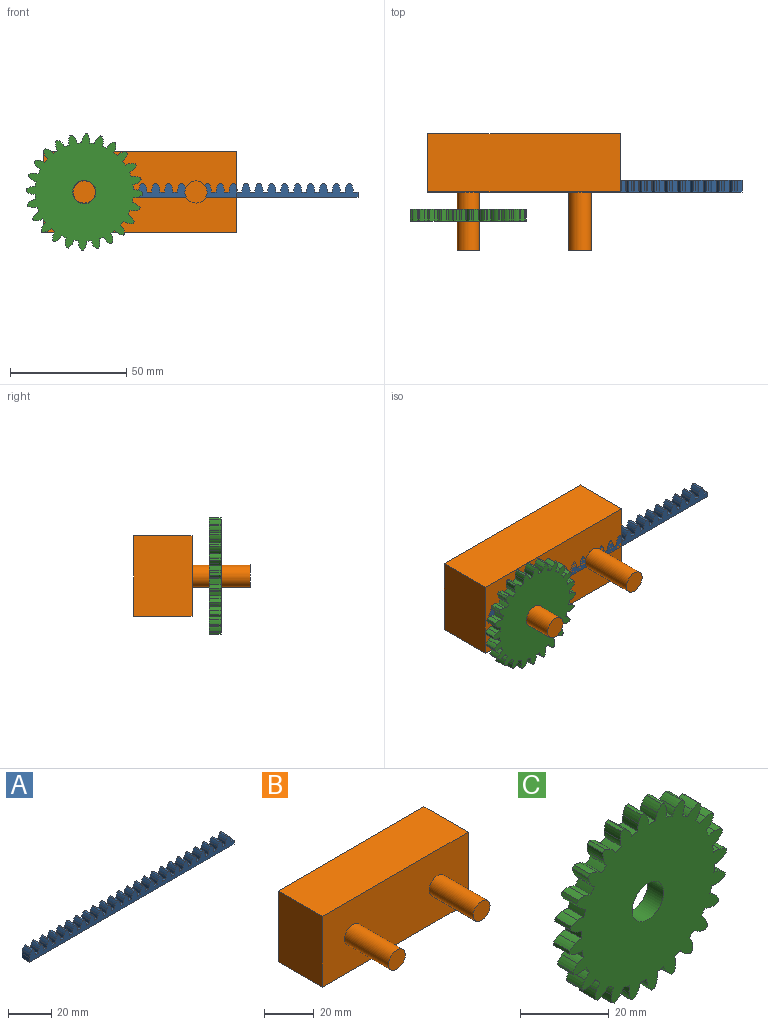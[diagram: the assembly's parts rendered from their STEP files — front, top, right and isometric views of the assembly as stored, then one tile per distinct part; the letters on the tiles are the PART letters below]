
ASSEMBLY  parts=3 mates=2
PART A: 173 faces, bbox 132.9x5x6.3 mm
  f0: cylinder r=5.39mm len=5mm, axis (0,1,0), area 10mm2, adj f1,f170,f171,f172
  f1: plane 5x2.01mm, normal (0,0,1), area 10mm2, adj f0,f2,f171,f172
  f2: plane 5x0mm, normal (1,0,0), area 0mm2, adj f1,f3,f171,f172
  f3: cylinder r=5.39mm len=5mm, axis (0,1,0), area 10mm2, adj f2,f4,f171,f172
  f4: cylinder r=6.11mm len=5mm, axis (0,1,0), area 11mm2, adj f3,f5,f171,f172
  f5: cylinder r=29.99mm len=5mm, axis (0,1,0), area 4.7mm2, adj f4,f6,f171,f172
  f6: cylinder r=6.16mm len=5mm, axis (0,1,0), area 11.1mm2, adj f5,f7,f171,f172
  f7: cylinder r=5.39mm len=5mm, axis (0,1,0), area 10mm2, adj f6,f8,f171,f172
  f8: plane 5x2.01mm, normal (0,0,1), area 10mm2, adj f7,f9,f171,f172
  f9: plane 5x0mm, normal (1,0,0), area 0mm2, adj f8,f10,f171,f172
  f10: cylinder r=5.39mm len=5mm, axis (0,1,0), area 10mm2, adj f9,f11,f171,f172
  f11: cylinder r=6.11mm len=5mm, axis (0,1,0), area 11mm2, adj f10,f12,f171,f172
  f12: cylinder r=29.99mm len=5mm, axis (0,1,0), area 4.7mm2, adj f11,f13,f171,f172
  f13: cylinder r=6.16mm len=5mm, axis (0,1,0), area 11.1mm2, adj f12,f14,f171,f172
  f14: cylinder r=5.39mm len=5mm, axis (0,1,0), area 10mm2, adj f13,f15,f171,f172
  f15: plane 5x2.01mm, normal (0,0,1), area 10mm2, adj f14,f16,f171,f172
  f16: plane 5x0mm, normal (1,0,0), area 0mm2, adj f15,f17,f171,f172
  f17: cylinder r=5.39mm len=5mm, axis (0,1,0), area 10mm2, adj f16,f18,f171,f172
  f18: cylinder r=6.11mm len=5mm, axis (0,1,0), area 11mm2, adj f17,f19,f171,f172
  f19: cylinder r=29.99mm len=5mm, axis (0,1,0), area 4.7mm2, adj f18,f20,f171,f172
  f20: cylinder r=6.16mm len=5mm, axis (0,1,0), area 11.1mm2, adj f19,f21,f171,f172
  f21: cylinder r=5.39mm len=5mm, axis (0,1,0), area 10mm2, adj f20,f22,f171,f172
  f22: plane 5x2.01mm, normal (0,0,1), area 10mm2, adj f21,f23,f171,f172
  f23: plane 5x0mm, normal (1,0,0), area 0mm2, adj f22,f24,f171,f172
  f24: cylinder r=5.39mm len=5mm, axis (0,1,0), area 10mm2, adj f23,f25,f171,f172
  f25: cylinder r=6.11mm len=5mm, axis (0,1,0), area 11mm2, adj f24,f26,f171,f172
  f26: cylinder r=29.99mm len=5mm, axis (0,1,0), area 4.7mm2, adj f25,f27,f171,f172
  f27: cylinder r=6.16mm len=5mm, axis (0,1,0), area 11.1mm2, adj f26,f28,f171,f172
  f28: cylinder r=5.39mm len=5mm, axis (0,1,0), area 10mm2, adj f27,f29,f171,f172
  f29: plane 5x2.01mm, normal (0,0,1), area 10mm2, adj f28,f30,f171,f172
  f30: plane 5x0mm, normal (1,0,0), area 0mm2, adj f29,f31,f171,f172
  f31: cylinder r=5.39mm len=5mm, axis (0,1,0), area 10mm2, adj f30,f32,f171,f172
  f32: cylinder r=6.11mm len=5mm, axis (0,1,0), area 11mm2, adj f31,f33,f171,f172
  f33: cylinder r=29.99mm len=5mm, axis (0,1,0), area 4.7mm2, adj f32,f34,f171,f172
  f34: cylinder r=6.16mm len=5mm, axis (0,1,0), area 11.1mm2, adj f33,f35,f171,f172
  f35: cylinder r=5.39mm len=5mm, axis (0,1,0), area 10mm2, adj f34,f36,f171,f172
  f36: plane 5x2.01mm, normal (0,0,1), area 10mm2, adj f35,f37,f171,f172
  f37: plane 5x0mm, normal (1,0,0), area 0mm2, adj f36,f38,f171,f172
  f38: cylinder r=5.39mm len=5mm, axis (0,1,0), area 10mm2, adj f37,f39,f171,f172
  f39: cylinder r=6.11mm len=5mm, axis (0,1,0), area 11mm2, adj f38,f40,f171,f172
  f40: cylinder r=29.99mm len=5mm, axis (0,1,0), area 4.7mm2, adj f39,f41,f171,f172
  f41: cylinder r=6.16mm len=5mm, axis (0,1,0), area 11.1mm2, adj f40,f42,f171,f172
  f42: cylinder r=5.39mm len=5mm, axis (0,1,0), area 10mm2, adj f41,f43,f171,f172
  f43: plane 5x2.01mm, normal (0,0,1), area 10mm2, adj f42,f44,f171,f172
  f44: plane 5x0mm, normal (1,0,0), area 0mm2, adj f43,f45,f171,f172
  f45: cylinder r=5.39mm len=5mm, axis (0,1,0), area 10mm2, adj f44,f46,f171,f172
  f46: cylinder r=6.11mm len=5mm, axis (0,1,0), area 11mm2, adj f45,f47,f171,f172
  f47: cylinder r=29.99mm len=5mm, axis (0,1,0), area 4.7mm2, adj f46,f48,f171,f172
  f48: cylinder r=6.16mm len=5mm, axis (0,1,0), area 11.1mm2, adj f47,f49,f171,f172
  f49: cylinder r=5.39mm len=5mm, axis (0,1,0), area 10mm2, adj f48,f50,f171,f172
  f50: plane 5x2.01mm, normal (0,0,1), area 10mm2, adj f49,f51,f171,f172
  f51: plane 5x0mm, normal (1,0,0), area 0mm2, adj f50,f52,f171,f172
  f52: cylinder r=5.39mm len=5mm, axis (0,1,0), area 10mm2, adj f51,f53,f171,f172
  f53: cylinder r=6.11mm len=5mm, axis (0,1,0), area 11mm2, adj f52,f54,f171,f172
  f54: cylinder r=29.99mm len=5mm, axis (0,1,0), area 4.7mm2, adj f53,f55,f171,f172
  f55: cylinder r=6.16mm len=5mm, axis (0,1,0), area 11.1mm2, adj f54,f56,f171,f172
  f56: cylinder r=5.39mm len=5mm, axis (0,1,0), area 10mm2, adj f55,f57,f171,f172
  f57: plane 5x2.01mm, normal (0,0,1), area 10mm2, adj f56,f58,f171,f172
  f58: plane 5x0mm, normal (1,0,0), area 0mm2, adj f57,f59,f171,f172
  f59: cylinder r=5.39mm len=5mm, axis (0,1,0), area 10mm2, adj f58,f60,f171,f172
  f60: cylinder r=6.11mm len=5mm, axis (0,1,0), area 11mm2, adj f59,f61,f171,f172
  f61: cylinder r=29.99mm len=5mm, axis (0,1,0), area 4.7mm2, adj f60,f62,f171,f172
  f62: cylinder r=6.16mm len=5mm, axis (0,1,0), area 11.1mm2, adj f61,f63,f171,f172
  f63: cylinder r=5.39mm len=5mm, axis (0,1,0), area 10mm2, adj f62,f64,f171,f172
  f64: plane 5x2.01mm, normal (0,0,1), area 10mm2, adj f63,f65,f171,f172
  f65: plane 5x0mm, normal (1,0,0), area 0mm2, adj f64,f66,f171,f172
  f66: cylinder r=5.39mm len=5mm, axis (0,1,0), area 10mm2, adj f65,f67,f171,f172
  f67: cylinder r=6.11mm len=5mm, axis (0,1,0), area 11mm2, adj f66,f68,f171,f172
  f68: cylinder r=29.99mm len=5mm, axis (0,1,0), area 4.7mm2, adj f67,f69,f171,f172
  f69: cylinder r=6.16mm len=5mm, axis (0,1,0), area 11.1mm2, adj f68,f70,f171,f172
  f70: cylinder r=5.39mm len=5mm, axis (0,1,0), area 10mm2, adj f69,f71,f171,f172
  f71: plane 5x2.01mm, normal (0,0,1), area 10mm2, adj f70,f72,f171,f172
  f72: plane 5x0mm, normal (1,0,0), area 0mm2, adj f71,f73,f171,f172
  f73: cylinder r=5.39mm len=5mm, axis (0,1,0), area 10mm2, adj f72,f74,f171,f172
  f74: cylinder r=6.11mm len=5mm, axis (0,1,0), area 11mm2, adj f73,f75,f171,f172
  f75: cylinder r=29.99mm len=5mm, axis (0,1,0), area 4.7mm2, adj f74,f76,f171,f172
  f76: cylinder r=6.16mm len=5mm, axis (0,1,0), area 11.1mm2, adj f75,f77,f171,f172
  f77: cylinder r=5.39mm len=5mm, axis (0,1,0), area 10mm2, adj f76,f78,f171,f172
  f78: plane 5x2.01mm, normal (0,0,1), area 10mm2, adj f77,f79,f171,f172
  f79: plane 5x0mm, normal (1,0,0), area 0mm2, adj f78,f80,f171,f172
  f80: cylinder r=5.39mm len=5mm, axis (0,1,0), area 10mm2, adj f79,f81,f171,f172
  f81: cylinder r=6.11mm len=5mm, axis (0,1,0), area 11mm2, adj f80,f82,f171,f172
  f82: cylinder r=29.99mm len=5mm, axis (0,1,0), area 4.7mm2, adj f81,f83,f171,f172
  f83: cylinder r=6.16mm len=5mm, axis (0,1,0), area 11.1mm2, adj f82,f84,f171,f172
  f84: cylinder r=5.39mm len=5mm, axis (0,1,0), area 10mm2, adj f83,f85,f171,f172
  f85: plane 5x2.01mm, normal (0,0,1), area 10mm2, adj f84,f86,f171,f172
  f86: plane 5x0mm, normal (1,0,0), area 0mm2, adj f85,f87,f171,f172
  f87: cylinder r=5.39mm len=5mm, axis (0,1,0), area 10mm2, adj f86,f88,f171,f172
  f88: cylinder r=6.11mm len=5mm, axis (0,1,0), area 11mm2, adj f87,f89,f171,f172
  f89: cylinder r=29.99mm len=5mm, axis (0,1,0), area 4.7mm2, adj f88,f90,f171,f172
  f90: cylinder r=6.16mm len=5mm, axis (0,1,0), area 11.1mm2, adj f89,f91,f171,f172
  f91: cylinder r=5.39mm len=5mm, axis (0,1,0), area 10mm2, adj f90,f92,f171,f172
  f92: plane 5x2.01mm, normal (0,0,1), area 10mm2, adj f91,f93,f171,f172
  f93: plane 5x0mm, normal (1,0,0), area 0mm2, adj f92,f94,f171,f172
  f94: cylinder r=5.39mm len=5mm, axis (0,1,0), area 10mm2, adj f93,f95,f171,f172
  f95: cylinder r=6.11mm len=5mm, axis (0,1,0), area 11mm2, adj f94,f96,f171,f172
  f96: cylinder r=29.99mm len=5mm, axis (0,1,0), area 4.7mm2, adj f95,f97,f171,f172
  f97: cylinder r=6.16mm len=5mm, axis (0,1,0), area 11.1mm2, adj f96,f98,f171,f172
  f98: cylinder r=5.39mm len=5mm, axis (0,1,0), area 10mm2, adj f97,f99,f171,f172
  f99: plane 5x2.01mm, normal (0,0,1), area 10mm2, adj f98,f100,f171,f172
  f100: plane 5x0mm, normal (1,0,0), area 0mm2, adj f99,f101,f171,f172
  f101: cylinder r=5.39mm len=5mm, axis (0,1,0), area 10mm2, adj f100,f102,f171,f172
  f102: cylinder r=6.11mm len=5mm, axis (0,1,0), area 11mm2, adj f101,f103,f171,f172
  f103: cylinder r=29.99mm len=5mm, axis (0,1,0), area 4.7mm2, adj f102,f104,f171,f172
  f104: cylinder r=6.16mm len=5mm, axis (0,1,0), area 11.1mm2, adj f103,f105,f171,f172
  f105: cylinder r=5.39mm len=5mm, axis (0,1,0), area 10mm2, adj f104,f106,f171,f172
  f106: plane 5x2.01mm, normal (0,0,1), area 10mm2, adj f105,f107,f171,f172
  f107: plane 5x0mm, normal (1,0,0), area 0mm2, adj f106,f108,f171,f172
  f108: cylinder r=5.39mm len=5mm, axis (0,1,0), area 10mm2, adj f107,f109,f171,f172
  f109: cylinder r=6.11mm len=5mm, axis (0,1,0), area 11mm2, adj f108,f110,f171,f172
  f110: cylinder r=29.99mm len=5mm, axis (0,1,0), area 4.7mm2, adj f109,f111,f171,f172
  f111: cylinder r=6.16mm len=5mm, axis (0,1,0), area 11.1mm2, adj f110,f112,f171,f172
  f112: cylinder r=5.39mm len=5mm, axis (0,1,0), area 10mm2, adj f111,f113,f171,f172
  f113: plane 5x2.01mm, normal (0,0,1), area 10mm2, adj f112,f114,f171,f172
  f114: plane 5x0mm, normal (1,0,0), area 0mm2, adj f113,f115,f171,f172
  f115: cylinder r=5.39mm len=5mm, axis (0,1,0), area 10mm2, adj f114,f116,f171,f172
  f116: cylinder r=6.11mm len=5mm, axis (0,1,0), area 11mm2, adj f115,f117,f171,f172
  f117: cylinder r=29.99mm len=5mm, axis (0,1,0), area 4.7mm2, adj f116,f118,f171,f172
  f118: cylinder r=6.16mm len=5mm, axis (0,1,0), area 11.1mm2, adj f117,f119,f171,f172
  f119: cylinder r=5.39mm len=5mm, axis (0,1,0), area 10mm2, adj f118,f120,f171,f172
  f120: plane 5x2.01mm, normal (0,0,1), area 10mm2, adj f119,f121,f171,f172
  f121: plane 5x0mm, normal (1,0,0), area 0mm2, adj f120,f122,f171,f172
  f122: cylinder r=5.39mm len=5mm, axis (0,1,0), area 10mm2, adj f121,f123,f171,f172
  f123: cylinder r=6.11mm len=5mm, axis (0,1,0), area 11mm2, adj f122,f124,f171,f172
  f124: cylinder r=29.99mm len=5mm, axis (0,1,0), area 4.7mm2, adj f123,f125,f171,f172
  f125: cylinder r=6.16mm len=5mm, axis (0,1,0), area 11.1mm2, adj f124,f126,f171,f172
  f126: cylinder r=5.39mm len=5mm, axis (0,1,0), area 10mm2, adj f125,f127,f171,f172
  f127: plane 5x2.01mm, normal (0,0,1), area 10mm2, adj f126,f128,f171,f172
  f128: plane 5x0mm, normal (1,0,0), area 0mm2, adj f127,f129,f171,f172
  f129: cylinder r=5.39mm len=5mm, axis (0,1,0), area 10mm2, adj f128,f130,f171,f172
  f130: cylinder r=6.11mm len=5mm, axis (0,1,0), area 11mm2, adj f129,f131,f171,f172
  f131: cylinder r=29.99mm len=5mm, axis (0,1,0), area 4.7mm2, adj f130,f132,f171,f172
  f132: cylinder r=6.16mm len=5mm, axis (0,1,0), area 11.1mm2, adj f131,f133,f171,f172
  f133: cylinder r=5.39mm len=5mm, axis (0,1,0), area 10mm2, adj f132,f134,f171,f172
  f134: plane 5x2.01mm, normal (0,0,1), area 10mm2, adj f133,f135,f171,f172
  f135: plane 5x0mm, normal (1,0,0), area 0mm2, adj f134,f136,f171,f172
  f136: cylinder r=5.39mm len=5mm, axis (0,1,0), area 10mm2, adj f135,f137,f171,f172
  f137: cylinder r=6.11mm len=5mm, axis (0,1,0), area 11mm2, adj f136,f138,f171,f172
  f138: cylinder r=29.99mm len=5mm, axis (0,1,0), area 4.7mm2, adj f137,f139,f171,f172
  f139: cylinder r=6.16mm len=5mm, axis (0,1,0), area 11.1mm2, adj f138,f140,f171,f172
  f140: cylinder r=5.39mm len=5mm, axis (0,1,0), area 10mm2, adj f139,f141,f171,f172
  f141: plane 5x2.01mm, normal (0,0,1), area 10mm2, adj f140,f142,f171,f172
  f142: plane 5x0mm, normal (1,0,0), area 0mm2, adj f141,f143,f171,f172
  f143: cylinder r=5.39mm len=5mm, axis (0,1,0), area 10mm2, adj f142,f144,f171,f172
  f144: cylinder r=6.11mm len=5mm, axis (0,1,0), area 11mm2, adj f143,f145,f171,f172
  f145: cylinder r=29.99mm len=5mm, axis (0,1,0), area 4.7mm2, adj f144,f146,f171,f172
  f146: cylinder r=6.16mm len=5mm, axis (0,1,0), area 11.1mm2, adj f145,f147,f171,f172
  f147: cylinder r=5.39mm len=5mm, axis (0,1,0), area 10mm2, adj f146,f148,f171,f172
  f148: plane 5x2.01mm, normal (0,0,1), area 10mm2, adj f147,f149,f171,f172
  f149: plane 5x0mm, normal (1,0,0), area 0mm2, adj f148,f150,f171,f172
  f150: cylinder r=5.39mm len=5mm, axis (0,1,0), area 10mm2, adj f149,f151,f171,f172
  f151: cylinder r=6.11mm len=5mm, axis (0,1,0), area 11mm2, adj f150,f152,f171,f172
  f152: cylinder r=29.99mm len=5mm, axis (0,1,0), area 4.7mm2, adj f151,f153,f171,f172
  f153: cylinder r=6.16mm len=5mm, axis (0,1,0), area 11.1mm2, adj f152,f154,f171,f172
  f154: cylinder r=5.39mm len=5mm, axis (0,1,0), area 10mm2, adj f153,f155,f171,f172
  f155: plane 5x2.01mm, normal (0,0,1), area 10mm2, adj f154,f156,f171,f172
  f156: plane 5x0mm, normal (1,0,0), area 0mm2, adj f155,f157,f171,f172
  f157: cylinder r=5.39mm len=5mm, axis (0,1,0), area 10mm2, adj f156,f158,f171,f172
  f158: cylinder r=6.11mm len=5mm, axis (0,1,0), area 11mm2, adj f157,f159,f171,f172
  f159: cylinder r=29.99mm len=5mm, axis (0,1,0), area 4.7mm2, adj f158,f160,f171,f172
  f160: cylinder r=6.16mm len=5mm, axis (0,1,0), area 11.1mm2, adj f159,f161,f171,f172
  f161: cylinder r=5.39mm len=5mm, axis (0,1,0), area 10mm2, adj f160,f162,f171,f172
  f162: plane 5x2.34mm, normal (-1,0,0), area 11.7mm2, adj f161,f163,f171,f172
  f163: plane 132.89x5mm, normal (0,0,-1), area 664.4mm2, adj f162,f164,f171,f172
  f164: plane 5x2.23mm, normal (1,0,0), area 11.1mm2, adj f163,f165,f171,f172
  f165: plane 5x2.01mm, normal (0,0,1), area 10mm2, adj f164,f166,f171,f172
  f166: plane 5x0mm, normal (1,0,0), area 0mm2, adj f165,f167,f171,f172
  f167: cylinder r=5.39mm len=5mm, axis (0,1,0), area 10mm2, adj f166,f168,f171,f172
  f168: cylinder r=6.11mm len=5mm, axis (0,1,0), area 11mm2, adj f167,f169,f171,f172
  f169: cylinder r=29.99mm len=5mm, axis (0,1,0), area 4.7mm2, adj f168,f170,f171,f172
  f170: cylinder r=6.16mm len=5mm, axis (0,1,0), area 11.1mm2, adj f0,f169,f171,f172
  f171: plane 132.9x6.26mm, normal (0,-1,0), area 563.7mm2, adj f0,f1,f2,f3,f4,f5,f6,f7
  f172: plane 132.9x6.26mm, normal (0,1,0), area 563.7mm2, adj f0,f1,f2,f3,f4,f5,f6,f7
PART B: 10 faces, bbox 82.7x50x34.7 mm
  f0: plane 82.71x25mm, normal (0,0,-1), area 2067.7mm2, adj f1,f3,f4,f5
  f1: plane 34.71x25mm, normal (1,0,0), area 867.7mm2, adj f0,f2,f4,f5
  f2: plane 82.71x25mm, normal (0,0,1), area 2067.7mm2, adj f1,f3,f4,f5
  f3: plane 34.71x25mm, normal (-1,0,0), area 867.7mm2, adj f0,f2,f4,f5
  f4: plane 82.71x34.71mm, normal (0,-1,0), area 2728.7mm2, adj f0,f1,f2,f3,f6,f8
  f5: plane 82.71x34.71mm, normal (0,1,0), area 2870.4mm2, adj f0,f1,f2,f3
  f6: cylinder r=4.75mm len=25mm, axis (0,1,0), area 746.1mm2, adj f4,f7
  f7: plane 9.5x9.5mm, normal (0,-1,0), area 70.9mm2, adj f6
  f8: cylinder r=4.75mm len=25mm, axis (0,1,0), area 746.1mm2, adj f4,f9
  f9: plane 9.5x9.5mm, normal (0,-1,0), area 70.9mm2, adj f8
PART C: 147 faces, bbox 49.9x5x49.9 mm
  f0: cylinder r=21.15mm len=5mm, axis (0,1,0), area 10mm2, adj f29,f30,f31,f91
  f1: cylinder r=21.15mm len=5mm, axis (0,1,0), area 10mm2, adj f30,f31,f86,f90
  f2: cylinder r=21.15mm len=5mm, axis (0,1,0), area 10mm2, adj f30,f31,f81,f85
  f3: cylinder r=21.15mm len=5mm, axis (0,1,0), area 10mm2, adj f30,f31,f76,f80
  f4: cylinder r=21.15mm len=5mm, axis (0,1,0), area 10mm2, adj f30,f31,f71,f75
  f5: cylinder r=21.15mm len=5mm, axis (0,1,0), area 10mm2, adj f30,f31,f66,f70
  f6: cylinder r=21.15mm len=5mm, axis (0,1,0), area 10mm2, adj f30,f31,f61,f65
  f7: cylinder r=21.15mm len=5mm, axis (0,1,0), area 10mm2, adj f30,f31,f56,f60
  f8: cylinder r=21.15mm len=5mm, axis (0,1,0), area 10mm2, adj f30,f31,f51,f55
  f9: cylinder r=21.15mm len=5mm, axis (0,1,0), area 10mm2, adj f30,f31,f46,f50
  f10: cylinder r=21.15mm len=5mm, axis (0,1,0), area 10mm2, adj f30,f31,f41,f45
  f11: cylinder r=21.15mm len=5mm, axis (0,1,0), area 10mm2, adj f30,f31,f36,f40
  f12: cylinder r=21.15mm len=5mm, axis (0,1,0), area 10mm2, adj f30,f31,f35,f142
  f13: cylinder r=21.15mm len=5mm, axis (0,1,0), area 10mm2, adj f30,f31,f141,f146
  f14: cylinder r=21.15mm len=5mm, axis (0,1,0), area 10mm2, adj f30,f31,f136,f140
  f15: cylinder r=21.15mm len=5mm, axis (0,1,0), area 10mm2, adj f30,f31,f131,f135
  f16: cylinder r=21.15mm len=5mm, axis (0,1,0), area 10mm2, adj f30,f31,f126,f130
  f17: cylinder r=21.15mm len=5mm, axis (0,1,0), area 10mm2, adj f30,f31,f121,f125
  f18: cylinder r=21.15mm len=5mm, axis (0,1,0), area 10mm2, adj f30,f31,f116,f120
  f19: cylinder r=21.15mm len=5mm, axis (0,1,0), area 10mm2, adj f30,f31,f111,f115
  f20: cylinder r=21.15mm len=5mm, axis (0,1,0), area 10mm2, adj f30,f31,f106,f110
  f21: cylinder r=21.15mm len=5mm, axis (0,1,0), area 10mm2, adj f30,f31,f101,f105
  f22: cylinder r=21.15mm len=5mm, axis (0,1,0), area 10mm2, adj f30,f31,f95,f100
  f23: cylinder r=21.15mm len=5mm, axis (0,1,0), area 10mm2, adj f24,f30,f31,f96
  f24: cylinder r=5.39mm len=5mm, axis (0,1,0), area 10mm2, adj f23,f25,f30,f31
  f25: cylinder r=6.11mm len=5mm, axis (0,1,0), area 11mm2, adj f24,f26,f30,f31
  f26: cylinder r=29.99mm len=5mm, axis (0,1,0), area 4.7mm2, adj f25,f27,f30,f31
  f27: cylinder r=6.16mm len=5mm, axis (0,1,0), area 11.1mm2, adj f26,f29,f30,f31
  f28: cylinder r=5mm len=10mm, axis (0,1,0), area 157.1mm2, adj f30,f31
  f29: cylinder r=5.39mm len=5mm, axis (0,1,0), area 10mm2, adj f0,f27,f30,f31
  f30: plane 49.91x49.91mm, normal (0,-1,0), area 1582.5mm2, adj f0,f1,f2,f3,f4,f5,f6,f7
  f31: plane 49.91x49.91mm, normal (0,1,0), area 1582.5mm2, adj f0,f1,f2,f3,f4,f5,f6,f7
  f32: cylinder r=6.11mm len=5mm, axis (0,1,0), area 11mm2, adj f30,f31,f33,f36
  f33: cylinder r=29.99mm len=5mm, axis (0,1,0), area 4.7mm2, adj f30,f31,f32,f34
  f34: cylinder r=6.16mm len=5mm, axis (0,1,0), area 11.1mm2, adj f30,f31,f33,f35
  f35: cylinder r=5.39mm len=5mm, axis (0,1,0), area 10mm2, adj f12,f30,f31,f34
  f36: cylinder r=5.39mm len=5mm, axis (0,1,0), area 10mm2, adj f11,f30,f31,f32
  f37: cylinder r=6.11mm len=5mm, axis (0,1,0), area 11mm2, adj f30,f31,f38,f41
  f38: cylinder r=29.99mm len=5mm, axis (0,1,0), area 4.7mm2, adj f30,f31,f37,f39
  f39: cylinder r=6.16mm len=5mm, axis (0,1,0), area 11.1mm2, adj f30,f31,f38,f40
  f40: cylinder r=5.39mm len=5mm, axis (0,1,0), area 10mm2, adj f11,f30,f31,f39
  f41: cylinder r=5.39mm len=5mm, axis (0,1,0), area 10mm2, adj f10,f30,f31,f37
  f42: cylinder r=6.11mm len=5mm, axis (0,1,0), area 11mm2, adj f30,f31,f43,f46
  f43: cylinder r=29.99mm len=5mm, axis (0,1,0), area 4.7mm2, adj f30,f31,f42,f44
  f44: cylinder r=6.16mm len=5mm, axis (0,1,0), area 11.1mm2, adj f30,f31,f43,f45
  f45: cylinder r=5.39mm len=5mm, axis (0,1,0), area 10mm2, adj f10,f30,f31,f44
  f46: cylinder r=5.39mm len=5mm, axis (0,1,0), area 10mm2, adj f9,f30,f31,f42
  f47: cylinder r=6.11mm len=5mm, axis (0,1,0), area 11mm2, adj f30,f31,f48,f51
  f48: cylinder r=29.99mm len=5mm, axis (0,1,0), area 4.7mm2, adj f30,f31,f47,f49
  f49: cylinder r=6.16mm len=5mm, axis (0,1,0), area 11.1mm2, adj f30,f31,f48,f50
  f50: cylinder r=5.39mm len=5mm, axis (0,1,0), area 10mm2, adj f9,f30,f31,f49
  f51: cylinder r=5.39mm len=5mm, axis (0,1,0), area 10mm2, adj f8,f30,f31,f47
  f52: cylinder r=6.11mm len=5mm, axis (0,1,0), area 11mm2, adj f30,f31,f53,f56
  f53: cylinder r=29.99mm len=5mm, axis (0,1,0), area 4.7mm2, adj f30,f31,f52,f54
  f54: cylinder r=6.16mm len=5mm, axis (0,1,0), area 11.1mm2, adj f30,f31,f53,f55
  f55: cylinder r=5.39mm len=5mm, axis (0,1,0), area 10mm2, adj f8,f30,f31,f54
  f56: cylinder r=5.39mm len=5mm, axis (0,1,0), area 10mm2, adj f7,f30,f31,f52
  f57: cylinder r=6.11mm len=5mm, axis (0,1,0), area 11mm2, adj f30,f31,f58,f61
  f58: cylinder r=29.99mm len=5mm, axis (0,1,0), area 4.7mm2, adj f30,f31,f57,f59
  f59: cylinder r=6.16mm len=5mm, axis (0,1,0), area 11.1mm2, adj f30,f31,f58,f60
  f60: cylinder r=5.39mm len=5mm, axis (0,1,0), area 10mm2, adj f7,f30,f31,f59
  f61: cylinder r=5.39mm len=5mm, axis (0,1,0), area 10mm2, adj f6,f30,f31,f57
  f62: cylinder r=6.11mm len=5mm, axis (0,1,0), area 11mm2, adj f30,f31,f63,f66
  f63: cylinder r=29.99mm len=5mm, axis (0,1,0), area 4.7mm2, adj f30,f31,f62,f64
  f64: cylinder r=6.16mm len=5mm, axis (0,1,0), area 11.1mm2, adj f30,f31,f63,f65
  f65: cylinder r=5.39mm len=5mm, axis (0,1,0), area 10mm2, adj f6,f30,f31,f64
  f66: cylinder r=5.39mm len=5mm, axis (0,1,0), area 10mm2, adj f5,f30,f31,f62
  f67: cylinder r=6.11mm len=5mm, axis (0,1,0), area 11mm2, adj f30,f31,f68,f71
  f68: cylinder r=29.99mm len=5mm, axis (0,1,0), area 4.7mm2, adj f30,f31,f67,f69
  f69: cylinder r=6.16mm len=5mm, axis (0,1,0), area 11.1mm2, adj f30,f31,f68,f70
  f70: cylinder r=5.39mm len=5mm, axis (0,1,0), area 10mm2, adj f5,f30,f31,f69
  f71: cylinder r=5.39mm len=5mm, axis (0,1,0), area 10mm2, adj f4,f30,f31,f67
  f72: cylinder r=6.11mm len=5mm, axis (0,1,0), area 11mm2, adj f30,f31,f73,f76
  f73: cylinder r=29.99mm len=5mm, axis (0,1,0), area 4.7mm2, adj f30,f31,f72,f74
  f74: cylinder r=6.16mm len=5mm, axis (0,1,0), area 11.1mm2, adj f30,f31,f73,f75
  f75: cylinder r=5.39mm len=5mm, axis (0,1,0), area 10mm2, adj f4,f30,f31,f74
  f76: cylinder r=5.39mm len=5mm, axis (0,1,0), area 10mm2, adj f3,f30,f31,f72
  f77: cylinder r=6.11mm len=5mm, axis (0,1,0), area 11mm2, adj f30,f31,f78,f81
  f78: cylinder r=29.99mm len=5mm, axis (0,1,0), area 4.7mm2, adj f30,f31,f77,f79
  f79: cylinder r=6.16mm len=5mm, axis (0,1,0), area 11.1mm2, adj f30,f31,f78,f80
  f80: cylinder r=5.39mm len=5mm, axis (0,1,0), area 10mm2, adj f3,f30,f31,f79
  f81: cylinder r=5.39mm len=5mm, axis (0,1,0), area 10mm2, adj f2,f30,f31,f77
  f82: cylinder r=6.11mm len=5mm, axis (0,1,0), area 11mm2, adj f30,f31,f83,f86
  f83: cylinder r=29.99mm len=5mm, axis (0,1,0), area 4.7mm2, adj f30,f31,f82,f84
  f84: cylinder r=6.16mm len=5mm, axis (0,1,0), area 11.1mm2, adj f30,f31,f83,f85
  f85: cylinder r=5.39mm len=5mm, axis (0,1,0), area 10mm2, adj f2,f30,f31,f84
  f86: cylinder r=5.39mm len=5mm, axis (0,1,0), area 10mm2, adj f1,f30,f31,f82
  f87: cylinder r=6.11mm len=5mm, axis (0,1,0), area 11mm2, adj f30,f31,f88,f91
  f88: cylinder r=29.99mm len=5mm, axis (0,1,0), area 4.7mm2, adj f30,f31,f87,f89
  f89: cylinder r=6.16mm len=5mm, axis (0,1,0), area 11.1mm2, adj f30,f31,f88,f90
  f90: cylinder r=5.39mm len=5mm, axis (0,1,0), area 10mm2, adj f1,f30,f31,f89
  f91: cylinder r=5.39mm len=5mm, axis (0,1,0), area 10mm2, adj f0,f30,f31,f87
  f92: cylinder r=6.11mm len=5mm, axis (0,1,0), area 11mm2, adj f30,f31,f93,f95
  f93: cylinder r=29.99mm len=5mm, axis (0,1,0), area 4.7mm2, adj f30,f31,f92,f94
  f94: cylinder r=6.16mm len=5mm, axis (0,1,0), area 11.1mm2, adj f30,f31,f93,f96
  f95: cylinder r=5.39mm len=5mm, axis (0,1,0), area 10mm2, adj f22,f30,f31,f92
  f96: cylinder r=5.39mm len=5mm, axis (0,1,0), area 10mm2, adj f23,f30,f31,f94
  f97: cylinder r=6.11mm len=5mm, axis (0,1,0), area 11mm2, adj f30,f31,f98,f101
  f98: cylinder r=29.99mm len=5mm, axis (0,1,0), area 4.7mm2, adj f30,f31,f97,f99
  f99: cylinder r=6.16mm len=5mm, axis (0,1,0), area 11.1mm2, adj f30,f31,f98,f100
  f100: cylinder r=5.39mm len=5mm, axis (0,1,0), area 10mm2, adj f22,f30,f31,f99
  f101: cylinder r=5.39mm len=5mm, axis (0,1,0), area 10mm2, adj f21,f30,f31,f97
  f102: cylinder r=6.11mm len=5mm, axis (0,1,0), area 11mm2, adj f30,f31,f103,f106
  f103: cylinder r=29.99mm len=5mm, axis (0,1,0), area 4.7mm2, adj f30,f31,f102,f104
  f104: cylinder r=6.16mm len=5mm, axis (0,1,0), area 11.1mm2, adj f30,f31,f103,f105
  f105: cylinder r=5.39mm len=5mm, axis (0,1,0), area 10mm2, adj f21,f30,f31,f104
  f106: cylinder r=5.39mm len=5mm, axis (0,1,0), area 10mm2, adj f20,f30,f31,f102
  f107: cylinder r=6.11mm len=5mm, axis (0,1,0), area 11mm2, adj f30,f31,f108,f111
  f108: cylinder r=29.99mm len=5mm, axis (0,1,0), area 4.7mm2, adj f30,f31,f107,f109
  f109: cylinder r=6.16mm len=5mm, axis (0,1,0), area 11.1mm2, adj f30,f31,f108,f110
  f110: cylinder r=5.39mm len=5mm, axis (0,1,0), area 10mm2, adj f20,f30,f31,f109
  f111: cylinder r=5.39mm len=5mm, axis (0,1,0), area 10mm2, adj f19,f30,f31,f107
  f112: cylinder r=6.11mm len=5mm, axis (0,1,0), area 11mm2, adj f30,f31,f113,f116
  f113: cylinder r=29.99mm len=5mm, axis (0,1,0), area 4.7mm2, adj f30,f31,f112,f114
  f114: cylinder r=6.16mm len=5mm, axis (0,1,0), area 11.1mm2, adj f30,f31,f113,f115
  f115: cylinder r=5.39mm len=5mm, axis (0,1,0), area 10mm2, adj f19,f30,f31,f114
  f116: cylinder r=5.39mm len=5mm, axis (0,1,0), area 10mm2, adj f18,f30,f31,f112
  f117: cylinder r=6.11mm len=5mm, axis (0,1,0), area 11mm2, adj f30,f31,f118,f121
  f118: cylinder r=29.99mm len=5mm, axis (0,1,0), area 4.7mm2, adj f30,f31,f117,f119
  f119: cylinder r=6.16mm len=5mm, axis (0,1,0), area 11.1mm2, adj f30,f31,f118,f120
  f120: cylinder r=5.39mm len=5mm, axis (0,1,0), area 10mm2, adj f18,f30,f31,f119
  f121: cylinder r=5.39mm len=5mm, axis (0,1,0), area 10mm2, adj f17,f30,f31,f117
  f122: cylinder r=6.11mm len=5mm, axis (0,1,0), area 11mm2, adj f30,f31,f123,f126
  f123: cylinder r=29.99mm len=5mm, axis (0,1,0), area 4.7mm2, adj f30,f31,f122,f124
  f124: cylinder r=6.16mm len=5mm, axis (0,1,0), area 11.1mm2, adj f30,f31,f123,f125
  f125: cylinder r=5.39mm len=5mm, axis (0,1,0), area 10mm2, adj f17,f30,f31,f124
  f126: cylinder r=5.39mm len=5mm, axis (0,1,0), area 10mm2, adj f16,f30,f31,f122
  f127: cylinder r=6.11mm len=5mm, axis (0,1,0), area 11mm2, adj f30,f31,f128,f131
  f128: cylinder r=29.99mm len=5mm, axis (0,1,0), area 4.7mm2, adj f30,f31,f127,f129
  f129: cylinder r=6.16mm len=5mm, axis (0,1,0), area 11.1mm2, adj f30,f31,f128,f130
  f130: cylinder r=5.39mm len=5mm, axis (0,1,0), area 10mm2, adj f16,f30,f31,f129
  f131: cylinder r=5.39mm len=5mm, axis (0,1,0), area 10mm2, adj f15,f30,f31,f127
  f132: cylinder r=6.11mm len=5mm, axis (0,1,0), area 11mm2, adj f30,f31,f133,f136
  f133: cylinder r=29.99mm len=5mm, axis (0,1,0), area 4.7mm2, adj f30,f31,f132,f134
  f134: cylinder r=6.16mm len=5mm, axis (0,1,0), area 11.1mm2, adj f30,f31,f133,f135
  f135: cylinder r=5.39mm len=5mm, axis (0,1,0), area 10mm2, adj f15,f30,f31,f134
  f136: cylinder r=5.39mm len=5mm, axis (0,1,0), area 10mm2, adj f14,f30,f31,f132
  f137: cylinder r=6.11mm len=5mm, axis (0,1,0), area 11mm2, adj f30,f31,f138,f141
  f138: cylinder r=29.99mm len=5mm, axis (0,1,0), area 4.7mm2, adj f30,f31,f137,f139
  f139: cylinder r=6.16mm len=5mm, axis (0,1,0), area 11.1mm2, adj f30,f31,f138,f140
  f140: cylinder r=5.39mm len=5mm, axis (0,1,0), area 10mm2, adj f14,f30,f31,f139
  f141: cylinder r=5.39mm len=5mm, axis (0,1,0), area 10mm2, adj f13,f30,f31,f137
  f142: cylinder r=5.39mm len=5mm, axis (0,1,0), area 10mm2, adj f12,f30,f31,f143
  f143: cylinder r=6.11mm len=5mm, axis (0,1,0), area 11mm2, adj f30,f31,f142,f144
  f144: cylinder r=29.99mm len=5mm, axis (0,1,0), area 4.7mm2, adj f30,f31,f143,f145
  f145: cylinder r=6.16mm len=5mm, axis (0,1,0), area 11.1mm2, adj f30,f31,f144,f146
  f146: cylinder r=5.39mm len=5mm, axis (0,1,0), area 10mm2, adj f13,f30,f31,f145
PLACE A t=(40.33,6.67,73.44)mm
PLACE B t=(93.22,26.67,-117.08)mm fixed
PLACE C rot(axis=(0,1,0),155.6deg) t=(-12.65,-8.33,3.97)mm
MATE slider A.f118 <-> B.f4  axis (0,-1,0) through (11.35,1.67,3.97)mm
MATE revolute C.f0 <-> B.f6  axis (0,1,0) through (-12.65,-10.83,3.97)mm
